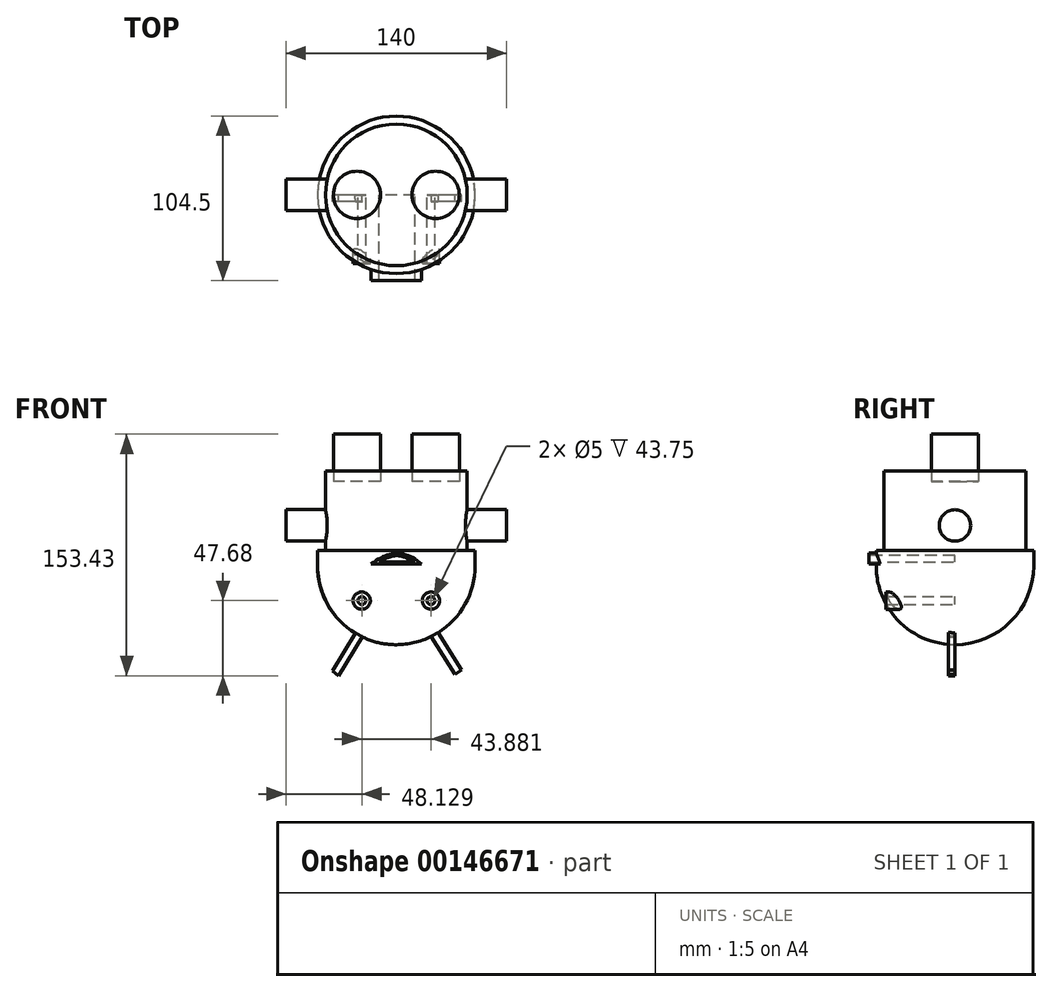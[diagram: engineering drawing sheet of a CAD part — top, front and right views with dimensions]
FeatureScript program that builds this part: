
annotation { "Feature Type Name" : "Feature", "Feature Type Description" : "" }
export const myFeature = defineFeature(function(context is Context, id is Id, definition is map)
    precondition{}
    {
        {
            var Q0;
            Q0=qCreatedBy(makeId("Top.planeOp"),FACE);
            var sketch = newSketch(context, id + "F0", { "sketchPlane" : qUnion([Q0])});
            skCircle(sketch, "E0", {"center": v(-25, 0) * mm, "radius": 15 * mm});
            skCircle(sketch, "E1", {"center": v(25, 0) * mm, "radius": 15 * mm});
            skSolve(sketch);
        }
        {
            var Q0;
            Q0=qCreatedBy(makeId("Top.planeOp"),FACE);
            var sketch = newSketch(context, id + "F1", { "sketchPlane" : qUnion([Q0])});
            skCircle(sketch, "E2", {"center": v(0, 0) * mm, "radius": 45 * mm});
            skSolve(sketch);
        }
        {
            var Q0;
            Q0=qCreatedBy(makeId("Top.planeOp"),FACE);
            var sketch = newSketch(context, id + "F2", { "sketchPlane" : qUnion([Q0])});
            skCircle(sketch, "E3", {"center": v(0, 0) * mm, "radius": 50 * mm});
            skSolve(sketch);
        }
        {
            var Q0;
            Q0=qSketchRegion(id+"F0",true);
            extrude(context, id + "F3", {"entities" : qUnion([Q0]), "depth" : 30 * mm});
        }
        {
            var Q0;
            Q0=makeQuery(id+"F1.imprint","IMPRINT",FACE,{"disambiguationData":[TD([[makeQuery(id+"F1.imprint","IMPRINT",EDGE,{"derivedFrom":sQuery(id+"F1.wireOp",EDGE,"E2")}),1.0]])]});
            extrude(context, id + "F4", {"entities" : qUnion([Q0]), "oppositeDirection" : true, "depth" : 50 * mm, "hasSecondDirection" : true, "secondDirectionOppositeDirection" : false, "secondDirectionDepth" : 6.5 * mm});
        }
        {
            var Q0;
            Q0=makeQuery(id+"F2.imprint","IMPRINT",FACE,{"disambiguationData":[TD([[makeQuery(id+"F2.imprint","IMPRINT",EDGE,{"derivedFrom":sQuery(id+"F2.wireOp",EDGE,"E3")}),1.0]])]});
            extrude(context, id + "F5", {"entities" : qUnion([Q0]), "operationType" : NewBodyOperationType.ADD, "oppositeDirection" : true, "depth" : 53.75 * mm, "hasSecondDirection" : true, "secondDirectionOppositeDirection" : true, "secondDirectionDepth" : 44 * mm});
        }
        {
            var Q0;
            Q0=qCreatedBy(makeId("Right.planeOp"),FACE);
            var sketch = newSketch(context, id + "F6", { "sketchPlane" : qUnion([Q0])});
            skCircle(sketch, "E4", {"center": v(0, -28) * mm, "radius": 10 * mm});
            skSolve(sketch);
        }
        {
            var Q0;
            Q0=qSketchRegion(id+"F6",true);
            extrude(context, id + "F7", {"entities" : qUnion([Q0]), "operationType" : NewBodyOperationType.ADD, "depth" : 70 * mm});
        }
        {
            var Q0;
            Q0=qCreatedBy(makeId("Right.planeOp"),FACE);
            var sketch = newSketch(context, id + "F8", { "sketchPlane" : qUnion([Q0])});
            skCircle(sketch, "E5", {"center": v(0, -28) * mm, "radius": 10 * mm});
            skSolve(sketch);
        }
        {
            var Q0;
            Q0=qSketchRegion(id+"F8",true);
            extrude(context, id + "F9", {"entities" : qUnion([Q0]), "operationType" : NewBodyOperationType.ADD, "oppositeDirection" : true, "depth" : 70 * mm});
        }
        {
            var Q0;
            Q0=qCreatedBy(makeId("Front.planeOp"),FACE);
            var sketch = newSketch(context, id + "F10", { "sketchPlane" : qUnion([Q0])});
            skArc(sketch, "E6", {"start": v(-50, -53.75) * mm, "mid": v(0, -103.75) * mm, "end": v(50, -53.75) * mm});
            skPoint(sketch, "E7", {"position": v(-50, -53.75) * mm});
            skLineSegment(sketch, "E8", {"start": v(-50, -53.75) * mm, "end": v(50, -53.75) * mm});
            skLineSegment(sketch, "E9", {"start": v(0, -53.75) * mm, "end": v(0, -103.75) * mm});
            skSolve(sketch);
        }
        {
            var Q0;
            {var subQ3=sQuery(id+"F10.wireOp",EDGE,"E9");Q0=makeQuery(id+"F10.imprint","IMPRINT",FACE,{"disambiguationData":[TD([[makeQuery(id+"F10.imprint","IMPRINT",EDGE,{"derivedFrom":subQ3}),1.0]])]});}
            var Q1;
            Q1=sQuery(id+"F10.wireOp",EDGE,"E9");
            revolve(context, id + "F11", {"operationType" : NewBodyOperationType.ADD, "entities" : qUnion([Q0]), "axis" : qUnion([Q1]), "revolveType" : RevolveType.FULL});
        }
        {
            var Q0;
            Q0=qCreatedBy(makeId("Front.planeOp"),FACE);
            var sketch = newSketch(context, id + "F12", { "sketchPlane" : qUnion([Q0])});
            skCircle(sketch, "E10", {"center": v(22, -75.75) * mm, "radius": 5.5 * mm});
            skCircle(sketch, "E11", {"center": v(-22, -75.75) * mm, "radius": 5.5 * mm});
            skSolve(sketch);
        }
        {
            var Q0;
            Q0=qSketchRegion(id+"F12",true);
            extrude(context, id + "F13", {"entities" : qUnion([Q0]), "operationType" : NewBodyOperationType.ADD, "depth" : 43.75 * mm});
        }
        {
            var Q0;
            Q0=qCreatedBy(makeId("Front.planeOp"),FACE);
            var sketch = newSketch(context, id + "F14", { "sketchPlane" : qUnion([Q0])});
            skCircle(sketch, "E12", {"center": v(22.01, -75.75) * mm, "radius": 2.5 * mm});
            skCircle(sketch, "E13", {"center": v(-21.87, -75.75) * mm, "radius": 2.5 * mm});
            skSolve(sketch);
        }
        {
            var Q0;
            Q0=qSketchRegion(id+"F14",true);
            extrude(context, id + "F15", {"entities" : qUnion([Q0]), "operationType" : NewBodyOperationType.REMOVE, "depth" : 50.5 * mm});
        }
        {
            var Q0;
            Q0=qCreatedBy(makeId("Front.planeOp"),FACE);
            var sketch = newSketch(context, id + "F16", { "sketchPlane" : qUnion([Q0])});
            skLineSegment(sketch, "E14", {"start": v(41.36, -119.85) * mm, "end": v(37.27, -122.74) * mm});
            skLineSegment(sketch, "E15", {"start": v(-36.73, -123.43) * mm, "end": v(-40.64, -120.32) * mm});
            skLineSegment(sketch, "E16", {"start": v(25.95, -95.29) * mm, "end": v(21.59, -97.74) * mm});
            skLineSegment(sketch, "E17", {"start": v(-25.58, -95.54) * mm, "end": v(-21.5, -98.43) * mm});
            skLineSegment(sketch, "E18", {"start": v(-21.5, -98.43) * mm, "end": v(-36.73, -123.43) * mm});
            skLineSegment(sketch, "E19", {"start": v(37.27, -122.74) * mm, "end": v(21.59, -97.74) * mm});
            skLineSegment(sketch, "E20", {"start": v(41.36, -119.85) * mm, "end": v(25.95, -95.29) * mm});
            skLineSegment(sketch, "E21", {"start": v(-25.58, -95.54) * mm, "end": v(-40.64, -120.32) * mm});
            skSolve(sketch);
        }
        {
            var Q0;
            Q0=qSketchRegion(id+"F16",true);
            extrude(context, id + "F17", {"entities" : qUnion([Q0]), "operationType" : NewBodyOperationType.ADD, "depth" : 4.25 * mm});
        }
        {
            var Q0;
            Q0=qCreatedBy(makeId("Front.planeOp"),FACE);
            var sketch = newSketch(context, id + "F18", { "sketchPlane" : qUnion([Q0])});
            skLineSegment(sketch, "E22", {"start": v(16, -52.62) * mm, "end": v(-16, -52.62) * mm});
            skFitSpline(sketch, "E23", {"points": [v(16, -52.62) * mm, v(0, -45.62) * mm, v(-16, -52.62) * mm], "startDerivative": vector(-32.35, 29.36) * mm, "endDerivative": vector(-39.65, -28.2) * mm});
            skSolve(sketch);
        }
        {
            var Q0;
            Q0 = qSketchRegion(id + "F18", true);
            extrude(context, id + "F19", {"entities" : qUnion([Q0]), "operationType" : NewBodyOperationType.ADD, "depth" : 54.5 * mm});
        }
        {
            var Q0;
            Q0=qCreatedBy(makeId("Front.planeOp"),FACE);
            var sketch = newSketch(context, id + "F20", { "sketchPlane" : qUnion([Q0])});
            skLineSegment(sketch, "E24", {"start": v(12, -51.22) * mm, "end": v(-11, -51.22) * mm});
            skFitSpline(sketch, "E25", {"points": [v(12, -51.22) * mm, v(0, -47.15) * mm, v(-11, -51.22) * mm], "startDerivative": vector(-24.67, 10.22) * mm, "endDerivative": vector(-23.3, -11.44) * mm});
            skSolve(sketch);
        }
        {
            var Q0;
            Q0 = qSketchRegion(id + "F20", true);
            extrude(context, id + "F21", {"entities" : qUnion([Q0]), "operationType" : NewBodyOperationType.REMOVE, "depth" : 63.5 * mm});
        }
    });
